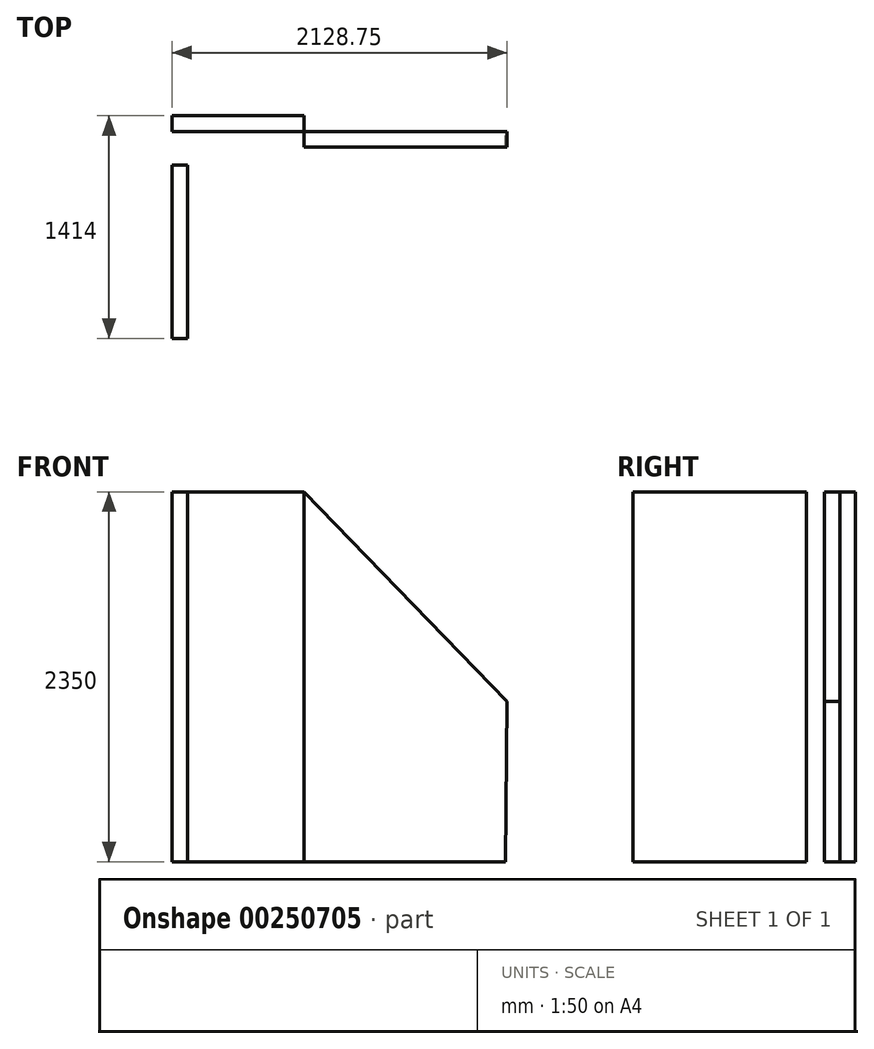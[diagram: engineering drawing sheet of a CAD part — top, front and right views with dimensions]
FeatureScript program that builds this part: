
annotation { "Feature Type Name" : "Feature", "Feature Type Description" : "" }
export const myFeature = defineFeature(function(context is Context, id is Id, definition is map)
    precondition{}
    {
        {
            var Q0;
            Q0=qCreatedBy(makeId("Top.planeOp"),FACE);
            var sketch = newSketch(context, id + "F0", { "sketchPlane" : qUnion([Q0])});
            skLineSegment(sketch, "E0.bottom", {"start": v(0, 1100) * mm, "end": v(100, 1100) * mm});
            skLineSegment(sketch, "E0.top", {"start": v(0, 0) * mm, "end": v(100, 0) * mm});
            skLineSegment(sketch, "E0.left", {"start": v(0, 1100) * mm, "end": v(0, 0) * mm});
            skLineSegment(sketch, "E0.right", {"start": v(100, 1100) * mm, "end": v(100, 0) * mm});
            skSolve(sketch);
        }
        {
            var Q0;
            Q0=makeQuery(id+"F0.imprint","IMPRINT",FACE,{"disambiguationData":[TD([[makeQuery(id+"F0.imprint","IMPRINT",EDGE,{"derivedFrom":sQuery(id+"F0.wireOp",EDGE,"E0.bottom")}),-1.0]])]});
            extrude(context, id + "F1", {"entities" : qUnion([Q0]), "depth" : 2350 * mm});
        }
        {
            var Q0;
            Q0=qCreatedBy(makeId("Top.planeOp"),FACE);
            var sketch = newSketch(context, id + "F2", { "sketchPlane" : qUnion([Q0])});
            skLineSegment(sketch, "E1.bottom", {"start": v(0, 1414) * mm, "end": v(840, 1414) * mm});
            skLineSegment(sketch, "E1.top", {"start": v(0, 1314) * mm, "end": v(840, 1314) * mm});
            skLineSegment(sketch, "E1.left", {"start": v(0, 1414) * mm, "end": v(0, 1314) * mm});
            skLineSegment(sketch, "E1.right", {"start": v(840, 1414) * mm, "end": v(840, 1314) * mm});
            skSolve(sketch);
        }
        {
            var Q0;
            Q0=makeQuery(id+"F2.imprint","IMPRINT",FACE,{"disambiguationData":[TD([[makeQuery(id+"F2.imprint","IMPRINT",EDGE,{"derivedFrom":sQuery(id+"F2.wireOp",EDGE,"E1.bottom")}),-1.0]])]});
            extrude(context, id + "F3", {"entities" : qUnion([Q0]), "depth" : 2350 * mm});
        }
        {
            var Q0;
            Q0=makeQuery(id+"F3.opExtrude","SWEPT_FACE",FACE,{"disambiguationData":[OSD([sQuery(id+"F2.wireOp",EDGE,"E1.top")])]});
            var sketch = newSketch(context, id + "F4", { "sketchPlane" : qUnion([Q0])});
            skLineSegment(sketch, "E2", {"start": v(840, 2350) * mm, "end": v(2128.75, 1019.96) * mm});
            skLineSegment(sketch, "E3", {"start": v(840, 0) * mm, "end": v(2120, 0) * mm});
            skLineSegment(sketch, "E4", {"start": v(2120, 0) * mm, "end": v(2128.75, 1019.96) * mm});
            skSolve(sketch);
        }
        {
            var Q0;
            Q0=makeQuery(id+"F4.imprint","IMPRINT",FACE,{"disambiguationData":[TD([[makeQuery(id+"F4.imprint","IMPRINT",EDGE,{"derivedFrom":sQuery(id+"F4.wireOp",EDGE,"E2")}),-1.0]])]});
            extrude(context, id + "F5", {"entities" : qUnion([Q0]), "depth" : 100 * mm});
        }
    });
